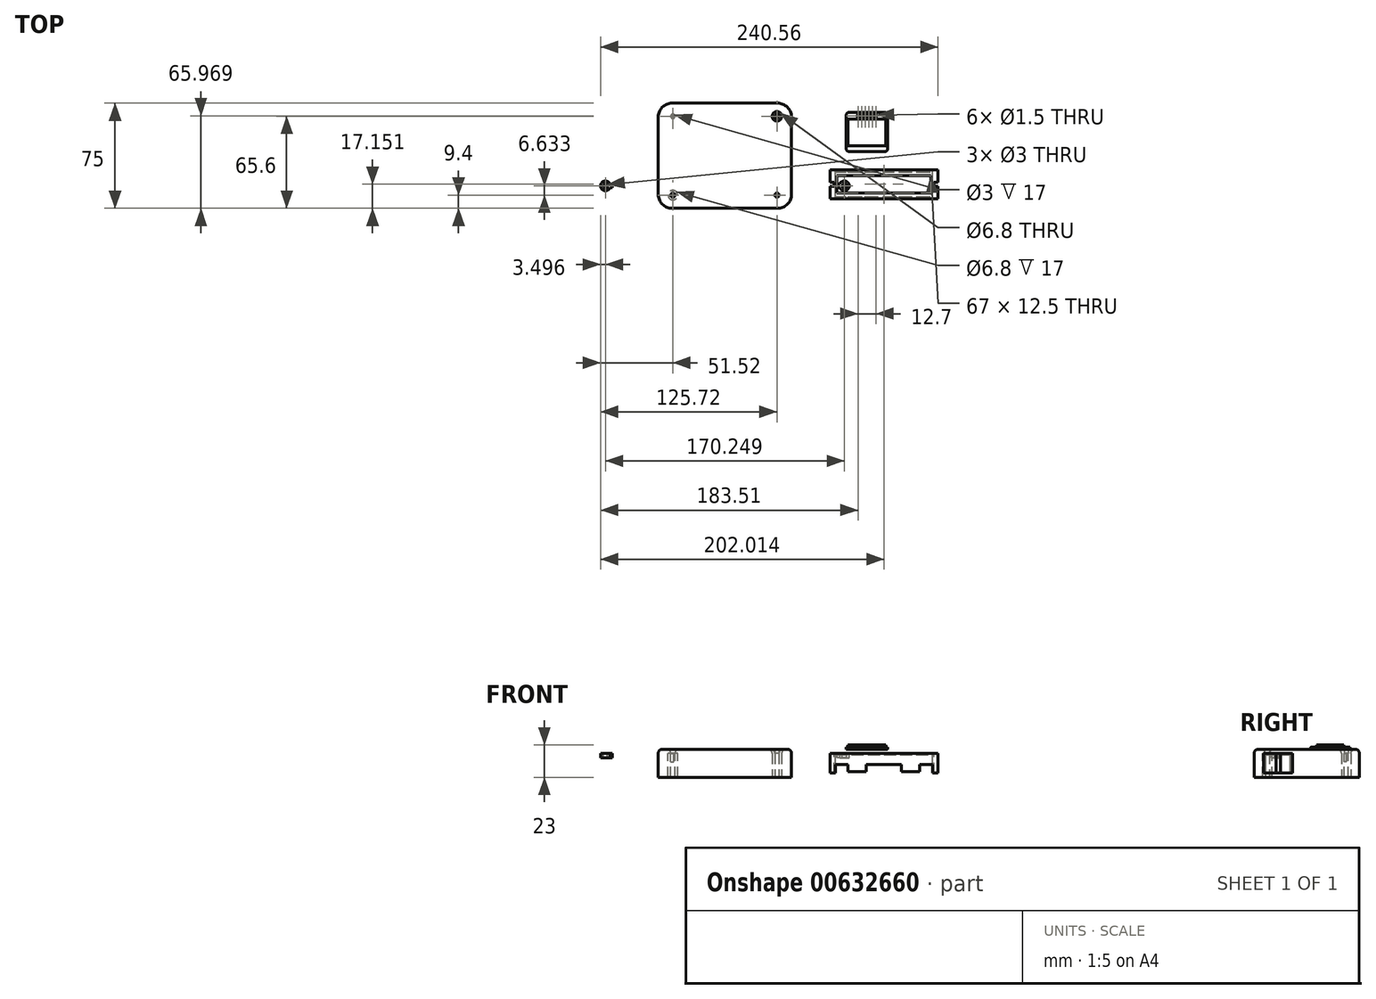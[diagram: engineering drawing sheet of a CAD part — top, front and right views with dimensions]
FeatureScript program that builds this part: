
annotation { "Feature Type Name" : "Feature", "Feature Type Description" : "" }
export const myFeature = defineFeature(function(context is Context, id is Id, definition is map)
    precondition{}
    {
        {
            var Q0;
            Q0=qCreatedBy(makeId("Top.planeOp"),FACE);
            var sketch = newSketch(context, id + "F0", { "sketchPlane" : qUnion([Q0])});
            skLineSegment(sketch, "E0.bottom", {"start": v(-37.5, -34.5) * mm, "end": v(37.5, -34.5) * mm});
            skLineSegment(sketch, "E0.top", {"start": v(-37.5, 34.5) * mm, "end": v(37.5, 34.5) * mm});
            skLineSegment(sketch, "E0.left", {"start": v(-44.5, -27.5) * mm, "end": v(-44.5, 27.5) * mm});
            skLineSegment(sketch, "E0.right", {"start": v(44.5, -27.5) * mm, "end": v(44.5, 27.5) * mm});
            skLineSegment(sketch, "E1", {"start": v(0, -34.5) * mm, "end": v(0, 34.5) * mm, "construction": true});
            skLineSegment(sketch, "E2", {"start": v(-44.5, 0) * mm, "end": v(44.5, 0) * mm, "construction": true});
            skCircle(sketch, "E3.MirrorC", {"center": v(37.1, 28.1) * mm, "radius": 3.4 * mm});
            skArc(sketch, "E4.MirrorC", {"start": v(-81.86, -22.72) * mm, "mid": v(-88.62, -21.47) * mm, "end": v(-81.86, -20.22) * mm});
            skPoint(sketch, "E5.visualSharp", {"position": v(-44.5, -34.5) * mm});
            skArc(sketch, "E5.filletArc", {"start": v(-44.5, -27.5) * mm, "mid": v(-42.45, -32.45) * mm, "end": v(-37.5, -34.5) * mm});
            skArc(sketch, "E6.MirrorCS", {"start": v(44.5, -27.5) * mm, "mid": v(42.45, -32.45) * mm, "end": v(37.5, -34.5) * mm});
            skArc(sketch, "E7.MirrorCS", {"start": v(-44.5, 27.5) * mm, "mid": v(-42.45, 32.45) * mm, "end": v(-37.5, 34.5) * mm});
            skArc(sketch, "E8.MirrorCS", {"start": v(44.5, 27.5) * mm, "mid": v(42.45, 32.45) * mm, "end": v(37.5, 34.5) * mm});
            skPoint(sketch, "E9.orphan", {"position": v(44.5, -34.5) * mm});
            skPoint(sketch, "E10.orphan", {"position": v(44.5, 34.5) * mm});
            skPoint(sketch, "E11.orphan", {"position": v(-44.5, 34.5) * mm});
            skArc(sketch, "E12.0", {"start": v(-47.5, -27.5) * mm, "mid": v(-44.57, -34.57) * mm, "end": v(-37.5, -37.5) * mm});
            skLineSegment(sketch, "E12.1", {"start": v(-47.5, -27.5) * mm, "end": v(-47.5, 27.5) * mm});
            skLineSegment(sketch, "E12.2", {"start": v(-37.5, -37.5) * mm, "end": v(37.5, -37.5) * mm});
            skArc(sketch, "E12.3", {"start": v(-47.5, 27.5) * mm, "mid": v(-44.57, 34.57) * mm, "end": v(-37.5, 37.5) * mm});
            skArc(sketch, "E12.4", {"start": v(47.5, -27.5) * mm, "mid": v(44.57, -34.57) * mm, "end": v(37.5, -37.5) * mm});
            skLineSegment(sketch, "E12.5", {"start": v(47.5, -27.5) * mm, "end": v(47.5, 27.5) * mm});
            skArc(sketch, "E12.6", {"start": v(47.5, 27.5) * mm, "mid": v(44.57, 34.57) * mm, "end": v(37.5, 37.5) * mm});
            skLineSegment(sketch, "E12.7", {"start": v(-37.5, 37.5) * mm, "end": v(37.5, 37.5) * mm});
            skPoint(sketch, "E13", {"position": v(0, 0) * mm});
            skCircle(sketch, "E14.MirrorC", {"center": v(-37.1, 28.1) * mm, "radius": 3.4 * mm});
            skLineSegment(sketch, "E15.bottom", {"start": v(-81.86, -22.72) * mm, "end": v(-80.12, -22.72) * mm});
            skLineSegment(sketch, "E15.top", {"start": v(-81.86, -20.22) * mm, "end": v(-80.12, -20.22) * mm});
            skLineSegment(sketch, "E15.right", {"start": v(-80.12, -22.72) * mm, "end": v(-80.12, -20.22) * mm});
            skArc(sketch, "E16.MirrorCS", {"start": v(81.86, -22.72) * mm, "mid": v(88.62, -21.47) * mm, "end": v(81.86, -20.22) * mm});
            skLineSegment(sketch, "E17.MirrorCS", {"start": v(81.86, -22.72) * mm, "end": v(80.12, -22.72) * mm});
            skLineSegment(sketch, "E18.MirrorCS", {"start": v(80.12, -22.72) * mm, "end": v(80.12, -20.22) * mm});
            skLineSegment(sketch, "E19.MirrorCS", {"start": v(81.86, -20.22) * mm, "end": v(80.12, -20.22) * mm});
            skCircle(sketch, "E20", {"center": v(-37.1, 28.1) * mm, "radius": 1.5 * mm});
            skCircle(sketch, "E21", {"center": v(37.1, 28.1) * mm, "radius": 1.5 * mm});
            skCircle(sketch, "E22", {"center": v(-85.12, -21.47) * mm, "radius": 1.5 * mm});
            skCircle(sketch, "E23", {"center": v(85.12, -21.47) * mm, "radius": 1.5 * mm});
            skCircle(sketch, "E24.MirrorC", {"center": v(-37.1, -28.1) * mm, "radius": 3.4 * mm});
            skCircle(sketch, "E25.MirrorC", {"center": v(-37.1, -28.1) * mm, "radius": 1.5 * mm});
            skLineSegment(sketch, "E26.MirrorCS", {"start": v(0, 34.5) * mm, "end": v(0, -34.5) * mm, "construction": true});
            skCircle(sketch, "E27.MirrorC", {"center": v(37.1, -28.1) * mm, "radius": 3.4 * mm});
            skCircle(sketch, "E28.MirrorC", {"center": v(37.1, -28.1) * mm, "radius": 1.5 * mm});
            skSolve(sketch);
        }
        {
            var Q0;
            Q0=makeQuery(id+"F0.imprint","IMPRINT",FACE,{"disambiguationData":[TD([[makeQuery(id+"F0.imprint","IMPRINT",EDGE,{"derivedFrom":sQuery(id+"F0.wireOp",EDGE,"E0.bottom")}),1.0]])]});
            var sketch = newSketch(context, id + "F1", { "sketchPlane" : qUnion([Q0])});
            skLineSegment(sketch, "E29.bottom", {"start": v(74.84, -30.7) * mm, "end": v(151.94, -30.7) * mm});
            skLineSegment(sketch, "E29.top", {"start": v(74.84, -10) * mm, "end": v(151.94, -10) * mm});
            skLineSegment(sketch, "E29.left", {"start": v(74.84, -30.7) * mm, "end": v(74.84, -21.85) * mm});
            skLineSegment(sketch, "E29.right", {"start": v(151.94, -30.7) * mm, "end": v(151.94, -21.85) * mm});
            skLineSegment(sketch, "E30", {"start": v(74.84, -20.35) * mm, "end": v(151.94, -20.35) * mm, "construction": true});
            skLineSegment(sketch, "E31", {"start": v(74.84, -10) * mm, "end": v(74.84, -18.85) * mm});
            skLineSegment(sketch, "E32", {"start": v(74.84, -18.85) * mm, "end": v(77.84, -18.85) * mm});
            skLineSegment(sketch, "E33", {"start": v(77.84, -18.85) * mm, "end": v(77.84, -21.85) * mm});
            skLineSegment(sketch, "E34", {"start": v(77.84, -21.85) * mm, "end": v(74.84, -21.85) * mm});
            skLineSegment(sketch, "E35", {"start": v(113.4, -10) * mm, "end": v(113.4, -30.7) * mm, "construction": true});
            skLineSegment(sketch, "E36.MirrorCS", {"start": v(148.94, -18.85) * mm, "end": v(148.94, -21.85) * mm});
            skLineSegment(sketch, "E37.MirrorCS", {"start": v(148.94, -21.85) * mm, "end": v(151.94, -21.85) * mm});
            skLineSegment(sketch, "E38.MirrorCS", {"start": v(151.94, -18.85) * mm, "end": v(148.94, -18.85) * mm});
            skLineSegment(sketch, "E39", {"start": v(77.84, -20.35) * mm, "end": v(76.06, -20.35) * mm});
            skLineSegment(sketch, "E40", {"start": v(78.84, -30.7) * mm, "end": v(78.84, -10) * mm});
            skLineSegment(sketch, "E41.MirrorCS", {"start": v(147.94, -30.7) * mm, "end": v(147.94, -10) * mm});
            skLineSegment(sketch, "E42", {"start": v(78.84, -11.6) * mm, "end": v(147.94, -11.6) * mm});
            skLineSegment(sketch, "E43.MirrorCS", {"start": v(78.84, -29.1) * mm, "end": v(138.94, -29.1) * mm});
            skLineSegment(sketch, "E44", {"start": v(87.84, -11.6) * mm, "end": v(87.84, -10) * mm});
            skLineSegment(sketch, "E45", {"start": v(100.84, -10) * mm, "end": v(100.84, -11.6) * mm});
            skLineSegment(sketch, "E46.MirrorCS", {"start": v(125.94, -10) * mm, "end": v(125.94, -11.6) * mm});
            skLineSegment(sketch, "E47.MirrorCS", {"start": v(138.94, -11.6) * mm, "end": v(138.94, -10) * mm});
            skLineSegment(sketch, "E48.MirrorCS", {"start": v(151.94, -20.35) * mm, "end": v(74.84, -20.35) * mm, "construction": true});
            skLineSegment(sketch, "E49.MirrorCS", {"start": v(87.84, -29.1) * mm, "end": v(87.84, -30.7) * mm});
            skLineSegment(sketch, "E50.MirrorCS", {"start": v(100.84, -30.7) * mm, "end": v(100.84, -29.1) * mm});
            skLineSegment(sketch, "E51.MirrorCS", {"start": v(125.94, -30.7) * mm, "end": v(125.94, -29.1) * mm});
            skLineSegment(sketch, "E52.MirrorCS", {"start": v(138.94, -29.1) * mm, "end": v(138.94, -30.7) * mm});
            skLineSegment(sketch, "E53.trimOffspring", {"start": v(74.84, -18.85) * mm, "end": v(74.84, -10) * mm});
            skLineSegment(sketch, "E54.trimOffspring", {"start": v(151.94, -18.85) * mm, "end": v(151.94, -10) * mm});
            skLineSegment(sketch, "E55.bottom", {"start": v(79.9, -26.6) * mm, "end": v(146.9, -26.6) * mm});
            skLineSegment(sketch, "E55.top", {"start": v(79.9, -14.1) * mm, "end": v(146.9, -14.1) * mm});
            skLineSegment(sketch, "E55.left", {"start": v(79.9, -26.6) * mm, "end": v(79.9, -14.1) * mm});
            skLineSegment(sketch, "E55.right", {"start": v(146.9, -26.6) * mm, "end": v(146.9, -14.1) * mm});
            skPoint(sketch, "E56", {"position": v(79.9, -20.35) * mm});
            skPoint(sketch, "E57", {"position": v(146.9, -20.35) * mm});
            skPoint(sketch, "E58", {"position": v(113.4, -26.6) * mm});
            skPoint(sketch, "E59", {"position": v(113.4, -14.1) * mm});
            skPoint(sketch, "E60.orphan", {"position": v(151.94, -29.1) * mm});
            skPoint(sketch, "E61.orphan", {"position": v(151.94, -11.6) * mm});
            skLineSegment(sketch, "E62", {"start": v(138.94, -29.1) * mm, "end": v(147.94, -29.1) * mm});
            skSolve(sketch);
        }
        {
            var Q0;
            Q0=makeQuery(id+"F0.imprint","IMPRINT",FACE,{"disambiguationData":[TD([[makeQuery(id+"F0.imprint","IMPRINT",EDGE,{"derivedFrom":sQuery(id+"F0.wireOp",EDGE,"E0.bottom")}),1.0]])]});
            var sketch = newSketch(context, id + "F2", { "sketchPlane" : qUnion([Q0])});
            skLineSegment(sketch, "E63.bottom", {"start": v(30, 33.7) * mm, "end": v(-40, 33.7) * mm});
            skLineSegment(sketch, "E63.top", {"start": v(30, -11.3) * mm, "end": v(-40, -11.3) * mm});
            skLineSegment(sketch, "E63.left", {"start": v(30, 33.7) * mm, "end": v(30, -11.3) * mm});
            skLineSegment(sketch, "E63.right", {"start": v(-40, 33.7) * mm, "end": v(-40, -11.3) * mm});
            skCircle(sketch, "E64", {"center": v(26, 29.7) * mm, "radius": 3 * mm});
            skCircle(sketch, "E65", {"center": v(26, 29.7) * mm, "radius": 1 * mm});
            skLineSegment(sketch, "E66", {"start": v(-5, 33.7) * mm, "end": v(-5, -11.3) * mm, "construction": true});
            skLineSegment(sketch, "E67", {"start": v(30, 11.2) * mm, "end": v(-40, 11.2) * mm, "construction": true});
            skCircle(sketch, "E68.MirrorC", {"center": v(-36, 29.7) * mm, "radius": 3 * mm});
            skCircle(sketch, "E69.MirrorC", {"center": v(-36, 29.7) * mm, "radius": 1 * mm});
            skCircle(sketch, "E70.MirrorC", {"center": v(26, -7.3) * mm, "radius": 1 * mm});
            skCircle(sketch, "E71.MirrorC", {"center": v(26, -7.3) * mm, "radius": 3 * mm});
            skCircle(sketch, "E72.MirrorC", {"center": v(-36, -7.3) * mm, "radius": 3 * mm});
            skCircle(sketch, "E73.MirrorC", {"center": v(-36, -7.3) * mm, "radius": 1 * mm});
            skLineSegment(sketch, "E74.bottom", {"start": v(-18, 19.7) * mm, "end": v(-45, 19.7) * mm});
            skLineSegment(sketch, "E74.top", {"start": v(-18, 3.7) * mm, "end": v(-45, 3.7) * mm});
            skLineSegment(sketch, "E74.left", {"start": v(-18, 19.7) * mm, "end": v(-18, 3.7) * mm});
            skLineSegment(sketch, "E74.right", {"start": v(-45, 19.7) * mm, "end": v(-45, 3.7) * mm});
            skPoint(sketch, "E75.firstSnap0", {"position": v(-18, 11.7) * mm});
            skLineSegment(sketch, "E76", {"start": v(-41, 19.7) * mm, "end": v(-41, 3.7) * mm});
            skSolve(sketch);
        }
        {
            var Q0;
            {var subQ0=sQuery(id+"F1.wireOp",EDGE,"E29.right");var subQ1=sQuery(id+"F1.wireOp",EDGE,"E29.bottom");var subQ2=makeQuery(id+"F1.imprint","INTERSECT",VERTEX,{"derivedFrom":[subQ1,subQ0]});Q0=makeQuery(id+"F1.imprint","IMPRINT",FACE,{"disambiguationData":[TD([[makeQuery(id+"F1.imprint","IMPRINT",EDGE,{"disambiguationData":[TD([[subQ2,1.0]])],"derivedFrom":subQ1}),1.0]])]});}
            var Q1;
            {var subQ0=sQuery(id+"F1.wireOp",EDGE,"E54.trimOffspring");var subQ1=sQuery(id+"F1.wireOp",EDGE,"E29.top");var subQ2=makeQuery(id+"F1.imprint","INTERSECT",VERTEX,{"derivedFrom":[subQ1,subQ0]});Q1=makeQuery(id+"F1.imprint","IMPRINT",FACE,{"disambiguationData":[TD([[makeQuery(id+"F1.imprint","IMPRINT",EDGE,{"disambiguationData":[TD([[subQ2,1.0]])],"derivedFrom":subQ1}),-1.0]])]});}
            var Q2;
            {var subQ3=sQuery(id+"F1.wireOp",EDGE,"E49.MirrorCS");Q2=makeQuery(id+"F1.imprint","IMPRINT",FACE,{"disambiguationData":[TD([[makeQuery(id+"F1.imprint","IMPRINT",EDGE,{"derivedFrom":subQ3}),-1.0]])]});}
            var Q3;
            {var subQ0=sQuery(id+"F1.wireOp",EDGE,"E49.MirrorCS");Q3=makeQuery(id+"F1.imprint","IMPRINT",FACE,{"disambiguationData":[TD([[makeQuery(id+"F1.imprint","IMPRINT",EDGE,{"derivedFrom":subQ0}),1.0]])]});}
            var Q4;
            {var subQ0=sQuery(id+"F1.wireOp",EDGE,"E50.MirrorCS");Q4=makeQuery(id+"F1.imprint","IMPRINT",FACE,{"disambiguationData":[TD([[makeQuery(id+"F1.imprint","IMPRINT",EDGE,{"derivedFrom":subQ0}),-1.0]])]});}
            var Q5;
            {var subQ0=sQuery(id+"F1.wireOp",EDGE,"E51.MirrorCS");Q5=makeQuery(id+"F1.imprint","IMPRINT",FACE,{"disambiguationData":[TD([[makeQuery(id+"F1.imprint","IMPRINT",EDGE,{"derivedFrom":subQ0}),-1.0]])]});}
            var Q6;
            {var subQ3=sQuery(id+"F1.wireOp",EDGE,"E52.MirrorCS");Q6=makeQuery(id+"F1.imprint","IMPRINT",FACE,{"disambiguationData":[TD([[makeQuery(id+"F1.imprint","IMPRINT",EDGE,{"derivedFrom":subQ3}),1.0]])]});}
            var Q7;
            {var subQ3=sQuery(id+"F1.wireOp",EDGE,"E44");Q7=makeQuery(id+"F1.imprint","IMPRINT",FACE,{"disambiguationData":[TD([[makeQuery(id+"F1.imprint","IMPRINT",EDGE,{"derivedFrom":subQ3}),1.0]])]});}
            var Q8;
            {var subQ0=sQuery(id+"F1.wireOp",EDGE,"E44");Q8=makeQuery(id+"F1.imprint","IMPRINT",FACE,{"disambiguationData":[TD([[makeQuery(id+"F1.imprint","IMPRINT",EDGE,{"derivedFrom":subQ0}),-1.0]])]});}
            var Q9;
            {var subQ0=sQuery(id+"F1.wireOp",EDGE,"E45");Q9=makeQuery(id+"F1.imprint","IMPRINT",FACE,{"disambiguationData":[TD([[makeQuery(id+"F1.imprint","IMPRINT",EDGE,{"derivedFrom":subQ0}),1.0]])]});}
            var Q10;
            {var subQ0=sQuery(id+"F1.wireOp",EDGE,"E46.MirrorCS");Q10=makeQuery(id+"F1.imprint","IMPRINT",FACE,{"disambiguationData":[TD([[makeQuery(id+"F1.imprint","IMPRINT",EDGE,{"derivedFrom":subQ0}),1.0]])]});}
            var Q11;
            {var subQ3=sQuery(id+"F1.wireOp",EDGE,"E47.MirrorCS");Q11=makeQuery(id+"F1.imprint","IMPRINT",FACE,{"disambiguationData":[TD([[makeQuery(id+"F1.imprint","IMPRINT",EDGE,{"derivedFrom":subQ3}),-1.0]])]});}
            var Q12;
            Q12=makeQuery(id+"F1.imprint","IMPRINT",FACE,{"disambiguationData":[TD([[makeQuery(id+"F1.imprint","IMPRINT",EDGE,{"derivedFrom":sQuery(id+"F1.wireOp",EDGE,"E36.MirrorCS")}),-1.0]])]});
            var Q13;
            {var subQ10=sQuery(id+"F1.wireOp",EDGE,"E29.left");Q13=makeQuery(id+"F1.imprint","IMPRINT",FACE,{"disambiguationData":[TD([[makeQuery(id+"F1.imprint","IMPRINT",EDGE,{"derivedFrom":subQ10}),-1.0]])]});}
            var Q14;
            Q14=makeQuery(id+"F1.imprint","IMPRINT",FACE,{"disambiguationData":[TD([[makeQuery(id+"F1.imprint","IMPRINT",EDGE,{"derivedFrom":sQuery(id+"F1.wireOp",EDGE,"E55.bottom")}),-1.0]])]});
            extrude(context, id + "F3", {"entities" : qUnion([Q0, Q1, Q2, Q3, Q4, Q5, Q6, Q7, Q8, Q9, Q10, Q11, Q12, Q13, Q14]), "depth" : -1 * mm, "offsetDistance" : 25 * mm});
        }
        {
            var Q0;
            {var subQ5=sQuery(id+"F1.wireOp",EDGE,"E29.left");Q0=makeQuery(id+"F1.imprint","IMPRINT",FACE,{"disambiguationData":[TD([[makeQuery(id+"F1.imprint","IMPRINT",EDGE,{"derivedFrom":subQ5}),-1.0]])]});}
            var Q1;
            {var subQ0=sQuery(id+"F1.wireOp",EDGE,"E29.right");Q1=makeQuery(id+"F1.imprint","IMPRINT",FACE,{"disambiguationData":[TD([[makeQuery(id+"F1.imprint","IMPRINT",EDGE,{"derivedFrom":subQ0}),1.0]])]});}
            extrude(context, id + "F4", {"entities" : qUnion([Q0, Q1]), "operationType" : NewBodyOperationType.ADD, "depth" : -14 * mm, "offsetDistance" : 25 * mm});
        }
        {
            var Q0;
            {var subQ3=sQuery(id+"F1.wireOp",EDGE,"E49.MirrorCS");Q0=makeQuery(id+"F1.imprint","IMPRINT",FACE,{"disambiguationData":[TD([[makeQuery(id+"F1.imprint","IMPRINT",EDGE,{"derivedFrom":subQ3}),-1.0]])]});}
            var Q1;
            {var subQ0=sQuery(id+"F1.wireOp",EDGE,"E50.MirrorCS");Q1=makeQuery(id+"F1.imprint","IMPRINT",FACE,{"disambiguationData":[TD([[makeQuery(id+"F1.imprint","IMPRINT",EDGE,{"derivedFrom":subQ0}),-1.0]])]});}
            var Q2;
            {var subQ3=sQuery(id+"F1.wireOp",EDGE,"E52.MirrorCS");Q2=makeQuery(id+"F1.imprint","IMPRINT",FACE,{"disambiguationData":[TD([[makeQuery(id+"F1.imprint","IMPRINT",EDGE,{"derivedFrom":subQ3}),1.0]])]});}
            var Q3;
            {var subQ3=sQuery(id+"F1.wireOp",EDGE,"E47.MirrorCS");Q3=makeQuery(id+"F1.imprint","IMPRINT",FACE,{"disambiguationData":[TD([[makeQuery(id+"F1.imprint","IMPRINT",EDGE,{"derivedFrom":subQ3}),-1.0]])]});}
            var Q4;
            {var subQ0=sQuery(id+"F1.wireOp",EDGE,"E45");Q4=makeQuery(id+"F1.imprint","IMPRINT",FACE,{"disambiguationData":[TD([[makeQuery(id+"F1.imprint","IMPRINT",EDGE,{"derivedFrom":subQ0}),1.0]])]});}
            var Q5;
            {var subQ3=sQuery(id+"F1.wireOp",EDGE,"E44");Q5=makeQuery(id+"F1.imprint","IMPRINT",FACE,{"disambiguationData":[TD([[makeQuery(id+"F1.imprint","IMPRINT",EDGE,{"derivedFrom":subQ3}),1.0]])]});}
            extrude(context, id + "F5", {"entities" : qUnion([Q0, Q1, Q2, Q3, Q4, Q5]), "operationType" : NewBodyOperationType.ADD, "depth" : -8 * mm, "offsetDistance" : 25 * mm});
        }
        {
            var Q0;
            {var subQ0=sQuery(id+"F1.wireOp",EDGE,"E49.MirrorCS");Q0=makeQuery(id+"F1.imprint","IMPRINT",FACE,{"disambiguationData":[TD([[makeQuery(id+"F1.imprint","IMPRINT",EDGE,{"derivedFrom":subQ0}),1.0]])]});}
            var Q1;
            {var subQ0=sQuery(id+"F1.wireOp",EDGE,"E51.MirrorCS");Q1=makeQuery(id+"F1.imprint","IMPRINT",FACE,{"disambiguationData":[TD([[makeQuery(id+"F1.imprint","IMPRINT",EDGE,{"derivedFrom":subQ0}),-1.0]])]});}
            var Q2;
            {var subQ0=sQuery(id+"F1.wireOp",EDGE,"E46.MirrorCS");Q2=makeQuery(id+"F1.imprint","IMPRINT",FACE,{"disambiguationData":[TD([[makeQuery(id+"F1.imprint","IMPRINT",EDGE,{"derivedFrom":subQ0}),1.0]])]});}
            var Q3;
            {var subQ0=sQuery(id+"F1.wireOp",EDGE,"E44");Q3=makeQuery(id+"F1.imprint","IMPRINT",FACE,{"disambiguationData":[TD([[makeQuery(id+"F1.imprint","IMPRINT",EDGE,{"derivedFrom":subQ0}),-1.0]])]});}
            extrude(context, id + "F6", {"entities" : qUnion([Q0, Q1, Q2, Q3]), "operationType" : NewBodyOperationType.ADD, "depth" : -13 * mm, "offsetDistance" : 25 * mm});
        }
        {
            var Q0;
            Q0=qSketchRegion(id+"F0",true);
            extrude(context, id + "F7", {"entities" : qUnion([Q0]), "oppositeDirection" : true, "depth" : 3 * mm, "offsetDistance" : 25 * mm});
        }
        {
            var Q0;
            Q0=makeQuery(id+"F0.imprint","IMPRINT",FACE,{"disambiguationData":[TD([[makeQuery(id+"F0.imprint","IMPRINT",EDGE,{"derivedFrom":sQuery(id+"F0.wireOp",EDGE,"E0.bottom")}),1.0]])]});
            var Q1;
            Q1=makeQuery(id+"F0.imprint","IMPRINT",FACE,{"disambiguationData":[TD([[makeQuery(id+"F0.imprint","IMPRINT",EDGE,{"derivedFrom":sQuery(id+"F0.wireOp",EDGE,"E0.bottom")}),-1.0]])]});
            var Q2;
            Q2=makeQuery(id+"F0.imprint","IMPRINT",FACE,{"disambiguationData":[TD([[makeQuery(id+"F0.imprint","IMPRINT",EDGE,{"derivedFrom":sQuery(id+"F0.wireOp",EDGE,"E24.MirrorC")}),-1.0]])]});
            var Q3;
            Q3=makeQuery(id+"F0.imprint","IMPRINT",FACE,{"disambiguationData":[TD([[makeQuery(id+"F0.imprint","IMPRINT",EDGE,{"derivedFrom":sQuery(id+"F0.wireOp",EDGE,"E25.MirrorC")}),-1.0]])]});
            var Q4;
            Q4=makeQuery(id+"F0.imprint","IMPRINT",FACE,{"disambiguationData":[TD([[makeQuery(id+"F0.imprint","IMPRINT",EDGE,{"derivedFrom":sQuery(id+"F0.wireOp",EDGE,"E27.MirrorC")}),1.0]])]});
            var Q5;
            Q5=makeQuery(id+"F0.imprint","IMPRINT",FACE,{"disambiguationData":[TD([[makeQuery(id+"F0.imprint","IMPRINT",EDGE,{"derivedFrom":sQuery(id+"F0.wireOp",EDGE,"E28.MirrorC")}),-1.0]])]});
            var Q6;
            Q6=makeQuery(id+"F0.imprint","IMPRINT",FACE,{"disambiguationData":[TD([[makeQuery(id+"F0.imprint","IMPRINT",EDGE,{"derivedFrom":sQuery(id+"F0.wireOp",EDGE,"E20")}),-1.0]])]});
            var Q7;
            Q7=makeQuery(id+"F0.imprint","IMPRINT",FACE,{"disambiguationData":[TD([[makeQuery(id+"F0.imprint","IMPRINT",EDGE,{"derivedFrom":sQuery(id+"F0.wireOp",EDGE,"E20")}),1.0]])]});
            var Q8;
            Q8=makeQuery(id+"F0.imprint","IMPRINT",FACE,{"disambiguationData":[TD([[makeQuery(id+"F0.imprint","IMPRINT",EDGE,{"derivedFrom":sQuery(id+"F0.wireOp",EDGE,"E3.MirrorC")}),-1.0]])]});
            var Q9;
            Q9=makeQuery(id+"F0.imprint","IMPRINT",FACE,{"disambiguationData":[TD([[makeQuery(id+"F0.imprint","IMPRINT",EDGE,{"derivedFrom":sQuery(id+"F0.wireOp",EDGE,"E21")}),1.0]])]});
            extrude(context, id + "F8", {"entities" : qUnion([Q0, Q1, Q2, Q3, Q4, Q5, Q6, Q7, Q8, Q9]), "operationType" : NewBodyOperationType.ADD, "depth" : 3 * mm, "offsetDistance" : 25 * mm});
        }
        {
            var Q0;
            Q0=makeQuery(id+"F0.imprint","IMPRINT",FACE,{"disambiguationData":[TD([[makeQuery(id+"F0.imprint","IMPRINT",EDGE,{"derivedFrom":sQuery(id+"F0.wireOp",EDGE,"E0.bottom")}),-1.0]])]});
            var Q1;
            Q1=makeQuery(id+"F0.imprint","IMPRINT",FACE,{"disambiguationData":[TD([[makeQuery(id+"F0.imprint","IMPRINT",EDGE,{"derivedFrom":sQuery(id+"F0.wireOp",EDGE,"E24.MirrorC")}),-1.0]])]});
            var Q2;
            Q2=makeQuery(id+"F0.imprint","IMPRINT",FACE,{"disambiguationData":[TD([[makeQuery(id+"F0.imprint","IMPRINT",EDGE,{"derivedFrom":sQuery(id+"F0.wireOp",EDGE,"E27.MirrorC")}),1.0]])]});
            var Q3;
            Q3=makeQuery(id+"F0.imprint","IMPRINT",FACE,{"disambiguationData":[TD([[makeQuery(id+"F0.imprint","IMPRINT",EDGE,{"derivedFrom":sQuery(id+"F0.wireOp",EDGE,"E3.MirrorC")}),-1.0]])]});
            var Q4;
            Q4=makeQuery(id+"F0.imprint","IMPRINT",FACE,{"disambiguationData":[TD([[makeQuery(id+"F0.imprint","IMPRINT",EDGE,{"derivedFrom":sQuery(id+"F0.wireOp",EDGE,"E20")}),-1.0]])]});
            extrude(context, id + "F9", {"entities" : qUnion([Q0, Q1, Q2, Q3, Q4]), "operationType" : NewBodyOperationType.ADD, "oppositeDirection" : true, "depth" : 17 * mm, "offsetDistance" : 25 * mm});
        }
        {
            var Q0;
            Q0=makeQuery(id+"F8.opExtrude","CAP_FACE",FACE,{"disambiguationData":[OSD([sQuery(id+"F0.wireOp",EDGE,"E12.0"),sQuery(id+"F0.wireOp",EDGE,"E12.1"),sQuery(id+"F0.wireOp",EDGE,"E12.2"),sQuery(id+"F0.wireOp",EDGE,"E12.3"),sQuery(id+"F0.wireOp",EDGE,"E12.4"),sQuery(id+"F0.wireOp",EDGE,"E12.5"),sQuery(id+"F0.wireOp",EDGE,"E12.6"),sQuery(id+"F0.wireOp",EDGE,"E12.7")])],"isStart":false});
            fillet(context, id + "F10", {"entities" : qUnion([Q0]), "radius" : 3 * mm, "tangentPropagation" : true, "allowEdgeOverflow" : false});
        }
        {
            var Q0;
            Q0=makeQuery(id+"F8.opExtrude","CAP_FACE",FACE,{"disambiguationData":[OSD([sQuery(id+"F0.wireOp",EDGE,"E12.0"),sQuery(id+"F0.wireOp",EDGE,"E12.1"),sQuery(id+"F0.wireOp",EDGE,"E12.2"),sQuery(id+"F0.wireOp",EDGE,"E12.3"),sQuery(id+"F0.wireOp",EDGE,"E12.4"),sQuery(id+"F0.wireOp",EDGE,"E12.5"),sQuery(id+"F0.wireOp",EDGE,"E12.6"),sQuery(id+"F0.wireOp",EDGE,"E12.7")])],"isStart":false});
            var sketch = newSketch(context, id + "F11", { "sketchPlane" : qUnion([Q0])});
            skLineSegment(sketch, "E77.bottom", {"start": v(113.94, 30.97) * mm, "end": v(88.54, 30.97) * mm});
            skLineSegment(sketch, "E77.top", {"start": v(113.94, 2.97) * mm, "end": v(88.54, 2.97) * mm});
            skLineSegment(sketch, "E77.left", {"start": v(115.94, 28.97) * mm, "end": v(115.94, 4.97) * mm});
            skLineSegment(sketch, "E77.right", {"start": v(86.54, 28.97) * mm, "end": v(86.54, 4.97) * mm});
            skLineSegment(sketch, "E78.bottom", {"start": v(114.64, 26.27) * mm, "end": v(87.84, 26.27) * mm});
            skLineSegment(sketch, "E78.top", {"start": v(114.64, 6.97) * mm, "end": v(87.84, 6.97) * mm});
            skLineSegment(sketch, "E78.left", {"start": v(114.64, 26.27) * mm, "end": v(114.64, 6.97) * mm});
            skLineSegment(sketch, "E78.right", {"start": v(87.84, 26.27) * mm, "end": v(87.84, 6.97) * mm});
            skCircle(sketch, "E79", {"center": v(105.05, 28.47) * mm, "radius": 0.75 * mm});
            skCircle(sketch, "E80", {"center": v(107.6, 28.47) * mm, "radius": 0.75 * mm});
            skLineSegment(sketch, "E81.bottom", {"start": v(108.74, 29.72) * mm, "end": v(93.74, 29.72) * mm, "construction": true});
            skLineSegment(sketch, "E81.top", {"start": v(108.74, 27.22) * mm, "end": v(93.74, 27.22) * mm, "construction": true});
            skLineSegment(sketch, "E81.left", {"start": v(108.74, 29.72) * mm, "end": v(108.74, 27.22) * mm, "construction": true});
            skLineSegment(sketch, "E81.right", {"start": v(93.74, 29.72) * mm, "end": v(93.74, 27.22) * mm, "construction": true});
            skLineSegment(sketch, "E82", {"start": v(108.74, 28.47) * mm, "end": v(93.74, 28.47) * mm, "construction": true});
            skCircle(sketch, "E83", {"center": v(102.51, 28.47) * mm, "radius": 0.75 * mm});
            skLineSegment(sketch, "E84", {"start": v(101.24, 27.22) * mm, "end": v(101.24, 29.72) * mm, "construction": true});
            skCircle(sketch, "E85.MirrorC", {"center": v(99.97, 28.47) * mm, "radius": 0.75 * mm});
            skCircle(sketch, "E86.MirrorC", {"center": v(97.43, 28.47) * mm, "radius": 0.75 * mm});
            skCircle(sketch, "E87.MirrorC", {"center": v(94.9, 28.47) * mm, "radius": 0.75 * mm});
            skLineSegment(sketch, "E88", {"start": v(101.24, 30.97) * mm, "end": v(101.24, 2.97) * mm, "construction": true});
            skLineSegment(sketch, "E89", {"start": v(114.64, 10.77) * mm, "end": v(87.84, 10.77) * mm});
            skPoint(sketch, "E90.visualSharp", {"position": v(115.94, 30.97) * mm});
            skArc(sketch, "E90.filletArc", {"start": v(115.94, 28.97) * mm, "mid": v(115.35, 30.38) * mm, "end": v(113.94, 30.97) * mm});
            skPoint(sketch, "E91.visualSharp", {"position": v(86.54, 30.97) * mm});
            skArc(sketch, "E91.filletArc", {"start": v(88.54, 30.97) * mm, "mid": v(87.13, 30.38) * mm, "end": v(86.54, 28.97) * mm});
            skPoint(sketch, "E92.visualSharp", {"position": v(115.94, 2.97) * mm});
            skArc(sketch, "E92.filletArc", {"start": v(113.94, 2.97) * mm, "mid": v(115.35, 3.55) * mm, "end": v(115.94, 4.97) * mm});
            skPoint(sketch, "E93.visualSharp", {"position": v(86.54, 2.97) * mm});
            skArc(sketch, "E93.filletArc", {"start": v(86.54, 4.97) * mm, "mid": v(87.13, 3.55) * mm, "end": v(88.54, 2.97) * mm});
            skLineSegment(sketch, "E94", {"start": v(101.24, 26.27) * mm, "end": v(101.24, 6.97) * mm, "construction": true});
            skLineSegment(sketch, "E95", {"start": v(115.94, 16.97) * mm, "end": v(86.54, 16.62) * mm});
            skPoint(sketch, "E95.endSnap0", {"position": v(87.84, 16.62) * mm});
            skSolve(sketch);
        }
        {
            var Q0;
            Q0=qSketchRegion(id+"F11",true);
            var Q1;
            {var subQ0=sQuery(id+"F11.wireOp",EDGE,"E78.bottom");Q1=makeQuery(id+"F11.imprint","IMPRINT",FACE,{"disambiguationData":[TD([[makeQuery(id+"F11.imprint","IMPRINT",EDGE,{"derivedFrom":subQ0}),1.0]])]});}
            var Q2;
            {var subQ0=sQuery(id+"F11.wireOp",EDGE,"E89");Q2=makeQuery(id+"F11.imprint","IMPRINT",FACE,{"disambiguationData":[TD([[makeQuery(id+"F11.imprint","IMPRINT",EDGE,{"derivedFrom":subQ0}),-1.0]])]});}
            var Q3;
            {var subQ0=sQuery(id+"F11.wireOp",EDGE,"E78.top");Q3=makeQuery(id+"F11.imprint","IMPRINT",FACE,{"disambiguationData":[TD([[makeQuery(id+"F11.imprint","IMPRINT",EDGE,{"derivedFrom":subQ0}),-1.0]])]});}
            extrude(context, id + "F12", {"entities" : qUnion([Q0, Q1, Q2, Q3]), "depth" : 1.6 * mm, "offsetDistance" : 25 * mm});
        }
        {
            var Q0;
            {var subQ0=sQuery(id+"F11.wireOp",EDGE,"E78.bottom");Q0=makeQuery(id+"F11.imprint","IMPRINT",FACE,{"disambiguationData":[TD([[makeQuery(id+"F11.imprint","IMPRINT",EDGE,{"derivedFrom":subQ0}),1.0]])]});}
            var Q1;
            {var subQ0=sQuery(id+"F11.wireOp",EDGE,"E89");Q1=makeQuery(id+"F11.imprint","IMPRINT",FACE,{"disambiguationData":[TD([[makeQuery(id+"F11.imprint","IMPRINT",EDGE,{"derivedFrom":subQ0}),-1.0]])]});}
            var Q2;
            {var subQ0=sQuery(id+"F11.wireOp",EDGE,"E78.top");Q2=makeQuery(id+"F11.imprint","IMPRINT",FACE,{"disambiguationData":[TD([[makeQuery(id+"F11.imprint","IMPRINT",EDGE,{"derivedFrom":subQ0}),-1.0]])]});}
            extrude(context, id + "F13", {"entities" : qUnion([Q0, Q1, Q2]), "operationType" : NewBodyOperationType.ADD, "depth" : 3 * mm, "offsetDistance" : 25 * mm});
        }
        {
            var Q0;
            Q0=makeQuery(id+"F2.imprint","IMPRINT",FACE,{"disambiguationData":[TD([[makeQuery(id+"F2.imprint","IMPRINT",EDGE,{"derivedFrom":sQuery(id+"F2.wireOp",EDGE,"E64")}),1.0]])]});
            var Q1;
            Q1=makeQuery(id+"F2.imprint","IMPRINT",FACE,{"disambiguationData":[TD([[makeQuery(id+"F2.imprint","IMPRINT",EDGE,{"derivedFrom":sQuery(id+"F2.wireOp",EDGE,"E68.MirrorC")}),-1.0]])]});
            var Q2;
            Q2=makeQuery(id+"F2.imprint","IMPRINT",FACE,{"disambiguationData":[TD([[makeQuery(id+"F2.imprint","IMPRINT",EDGE,{"derivedFrom":sQuery(id+"F2.wireOp",EDGE,"E70.MirrorC")}),1.0]])]});
            var Q3;
            Q3=makeQuery(id+"F2.imprint","IMPRINT",FACE,{"disambiguationData":[TD([[makeQuery(id+"F2.imprint","IMPRINT",EDGE,{"derivedFrom":sQuery(id+"F2.wireOp",EDGE,"E72.MirrorC")}),1.0]])]});
            extrude(context, id + "F14", {"entities" : qUnion([Q0, Q1, Q2, Q3]), "operationType" : NewBodyOperationType.ADD, "oppositeDirection" : true, "depth" : 6 * mm, "offsetDistance" : 25 * mm});
        }
    });
